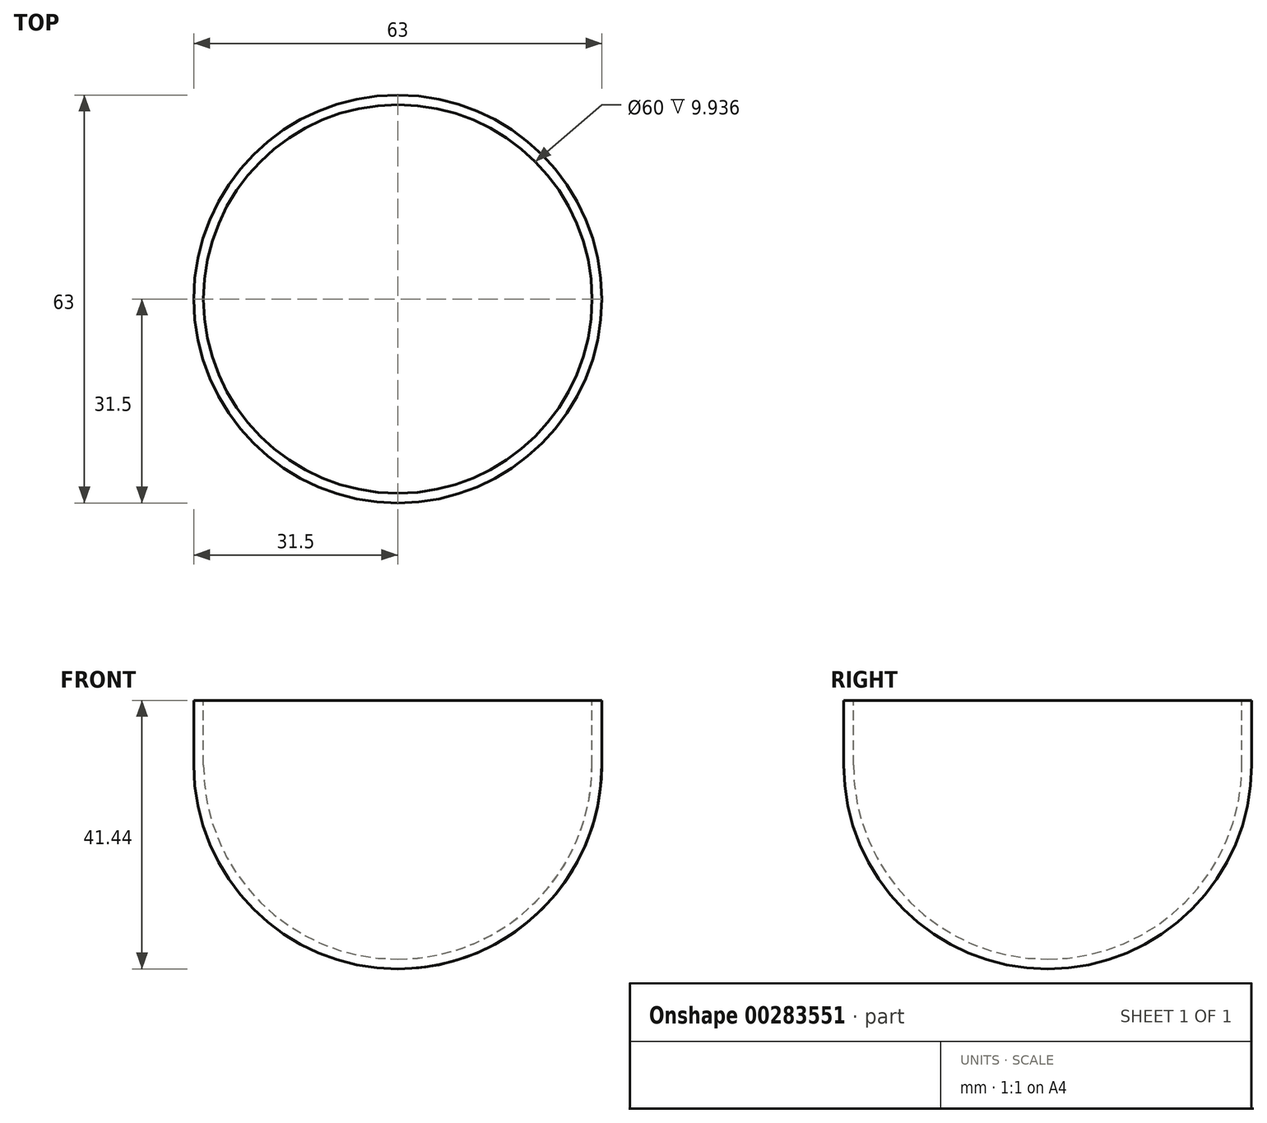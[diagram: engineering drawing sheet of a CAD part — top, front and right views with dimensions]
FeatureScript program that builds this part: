
annotation { "Feature Type Name" : "Feature", "Feature Type Description" : "" }
export const myFeature = defineFeature(function(context is Context, id is Id, definition is map)
    precondition{}
    {
        {
            var Q0;
            Q0=qCreatedBy(makeId("Front.planeOp"),FACE);
            var sketch = newSketch(context, id + "F0", { "sketchPlane" : qUnion([Q0])});
            skLineSegment(sketch, "E0", {"start": v(33, 33) * mm, "end": v(33, 50) * mm});
            skLineSegment(sketch, "E1", {"start": v(33, 33) * mm, "end": v(33, 0) * mm, "construction": true});
            skLineSegment(sketch, "E2", {"start": v(0, 75) * mm, "end": v(0, 33) * mm, "construction": true});
            skLineSegment(sketch, "E3", {"start": v(0, 0) * mm, "end": v(0, 6.53) * mm});
            skArc(sketch, "E4", {"start": v(0, 0) * mm, "mid": v(23.33, 9.67) * mm, "end": v(33, 33) * mm});
            skArc(sketch, "E5.0", {"start": v(0, 3) * mm, "mid": v(21.21, 11.79) * mm, "end": v(30, 33) * mm});
            skLineSegment(sketch, "E6", {"start": v(30, 33) * mm, "end": v(30, 50) * mm});
            skLineSegment(sketch, "E7", {"start": v(30, 50) * mm, "end": v(30, 50) * mm});
            skPoint(sketch, "E8.orphan", {"position": v(33, 50) * mm});
            skLineSegment(sketch, "E9", {"start": v(21.21, 11.79) * mm, "end": v(22.27, 10.73) * mm, "construction": true});
            skLineSegment(sketch, "E10", {"start": v(31.5, 33) * mm, "end": v(30, 33) * mm});
            skLineSegment(sketch, "E11", {"start": v(30, 50) * mm, "end": v(31.5, 50) * mm});
            skLineSegment(sketch, "E12", {"start": v(31.7, 50) * mm, "end": v(31.7, 55) * mm, "construction": true});
            skLineSegment(sketch, "E13", {"start": v(31.7, 55) * mm, "end": v(31.7, 72) * mm});
            skLineSegment(sketch, "E14", {"start": v(31.7, 72) * mm, "end": v(30.7, 72) * mm});
            skLineSegment(sketch, "E15", {"start": v(30.7, 72) * mm, "end": v(30.7, 55) * mm});
            skLineSegment(sketch, "E16", {"start": v(30.7, 55) * mm, "end": v(31.7, 55) * mm});
            skLineSegment(sketch, "E17", {"start": v(31.7, 63.5) * mm, "end": v(22.7, 63.5) * mm, "construction": true});
            skPoint(sketch, "E17.endSnap0", {"position": v(31.7, 63.5) * mm});
            skLineSegment(sketch, "E18", {"start": v(22.7, 63.5) * mm, "end": v(22.7, 72) * mm});
            skLineSegment(sketch, "E19", {"start": v(22.7, 63.5) * mm, "end": v(22.7, 55) * mm});
            skLineSegment(sketch, "E20", {"start": v(22.7, 55) * mm, "end": v(23.7, 55) * mm});
            skLineSegment(sketch, "E21", {"start": v(23.7, 55) * mm, "end": v(23.7, 63.5) * mm});
            skLineSegment(sketch, "E22", {"start": v(22.7, 55) * mm, "end": v(22.2, 55) * mm});
            skLineSegment(sketch, "E23", {"start": v(22.2, 55) * mm, "end": v(22.2, 72) * mm});
            skLineSegment(sketch, "E24", {"start": v(22.2, 72) * mm, "end": v(22.7, 72) * mm});
            skArc(sketch, "E25", {"start": v(0, 31.3) * mm, "mid": v(16.76, 38.24) * mm, "end": v(23.7, 55) * mm});
            skArc(sketch, "E26.0", {"start": v(0, 32.8) * mm, "mid": v(15.7, 39.3) * mm, "end": v(22.2, 55) * mm});
            skLineSegment(sketch, "E27", {"start": v(0, 32.8) * mm, "end": v(0, 31.3) * mm});
            skLineSegment(sketch, "E28", {"start": v(31.5, 33) * mm, "end": v(31.7, 33) * mm});
            skLineSegment(sketch, "E29", {"start": v(31.7, 33) * mm, "end": v(31.7, 50) * mm});
            skLineSegment(sketch, "E30.trimOffspring", {"start": v(0, 32.8) * mm, "end": v(0, 0) * mm, "construction": true});
            skLineSegment(sketch, "E31", {"start": v(23.7, 63.5) * mm, "end": v(23.7, 55) * mm});
            skLineSegment(sketch, "E32", {"start": v(23.7, 59.25) * mm, "end": v(28.8, 59.23) * mm, "construction": true});
            skLineSegment(sketch, "E33", {"start": v(23.7, 59.25) * mm, "end": v(25.4, 59.25) * mm, "construction": true});
            skLineSegment(sketch, "E34", {"start": v(23.64, 59.25) * mm, "end": v(25.34, 59.24) * mm, "construction": true});
            skLineSegment(sketch, "E35", {"start": v(25.4, 59.25) * mm, "end": v(25.4, 61.45) * mm, "construction": true});
            skLineSegment(sketch, "E36", {"start": v(23.64, 59.25) * mm, "end": v(23.64, 57.05) * mm, "construction": true});
            skFitSpline(sketch, "E37", {"points": [v(23.7, 59.25) * mm, v(24.3, 60.78) * mm, v(25.4, 61.45) * mm], "startDerivative": vector(0, 1.77) * mm, "endDerivative": vector(2.28, 0.15) * mm});
            skLineSegment(sketch, "E38", {"start": v(23.7, 59.25) * mm, "end": v(24.2, 59.25) * mm});
            skLineSegment(sketch, "E39", {"start": v(25.4, 61.45) * mm, "end": v(25.4, 60.95) * mm});
            skFitSpline(sketch, "E40", {"points": [v(24.2, 59.25) * mm, v(24.56, 60.34) * mm, v(25.4, 60.95) * mm], "startDerivative": vector(0.07, 1.51) * mm, "endDerivative": vector(2.13, 0.19) * mm});
            skFitSpline(sketch, "E41", {"points": [v(25.4, 60.95) * mm, v(26.43, 60.35) * mm, v(26.85, 59.25) * mm], "startDerivative": vector(2.26, -0.06) * mm, "endDerivative": vector(0.1, -2.09) * mm});
            skFitSpline(sketch, "E42", {"points": [v(25.4, 61.45) * mm, v(26.6, 60.89) * mm, v(27.35, 59.25) * mm], "startDerivative": vector(2.58, -0.22) * mm, "endDerivative": vector(-0.05, -2.13) * mm});
            skFitSpline(sketch, "E43.MirrorCS", {"points": [v(28.8, 57.55) * mm, v(27.77, 58.15) * mm, v(27.35, 59.25) * mm], "startDerivative": vector(-2.26, 0.06) * mm, "endDerivative": vector(-0.1, 2.09) * mm});
            skFitSpline(sketch, "E44.MirrorCS", {"points": [v(28.8, 57.05) * mm, v(27.6, 57.61) * mm, v(26.85, 59.25) * mm], "startDerivative": vector(-2.58, 0.22) * mm, "endDerivative": vector(0.05, 2.13) * mm});
            skFitSpline(sketch, "E45.MirrorCS", {"points": [v(30.29, 59.23) * mm, v(29.97, 58.34) * mm, v(28.8, 57.55) * mm], "startDerivative": vector(-0.07, -1.51) * mm, "endDerivative": vector(-2.13, -0.19) * mm});
            skFitSpline(sketch, "E46.MirrorCS", {"points": [v(30.7, 59.26) * mm, v(30.25, 58) * mm, v(28.8, 57.05) * mm], "startDerivative": vector(0, -1.77) * mm, "endDerivative": vector(-2.28, -0.15) * mm});
            skLineSegment(sketch, "E47", {"start": v(24.07, 58.94) * mm, "end": v(23.96, 58.52) * mm});
            skLineSegment(sketch, "E48", {"start": v(23.96, 58.52) * mm, "end": v(23.84, 58.07) * mm});
            skLineSegment(sketch, "E49", {"start": v(23.84, 58.07) * mm, "end": v(23.78, 57.67) * mm});
            skLineSegment(sketch, "E50", {"start": v(23.78, 57.67) * mm, "end": v(23.7, 57.12) * mm});
            skLineSegment(sketch, "E51", {"start": v(24.07, 58.94) * mm, "end": v(24.31, 59.78) * mm});
            skLineSegment(sketch, "E52", {"start": v(27.1, 59.25) * mm, "end": v(27.1, 57.68) * mm});
            skLineSegment(sketch, "E53", {"start": v(30.5, 59.71) * mm, "end": v(30.63, 60.43) * mm});
            skLineSegment(sketch, "E54", {"start": v(30.63, 60.43) * mm, "end": v(30.7, 61.23) * mm});
            skLineSegment(sketch, "E55", {"start": v(30.5, 59.71) * mm, "end": v(30.36, 59.23) * mm});
            skLineSegment(sketch, "E56", {"start": v(30.36, 59.23) * mm, "end": v(30.18, 58.73) * mm});
            skLineSegment(sketch, "E57", {"start": v(23.7, 63.5) * mm, "end": v(22.7, 63.5) * mm});
            skLineSegment(sketch, "E58", {"start": v(22.2, 72) * mm, "end": v(0, 72) * mm, "construction": true});
            skLineSegment(sketch, "E59", {"start": v(31.7, 33) * mm, "end": v(32, 33) * mm});
            skLineSegment(sketch, "E60", {"start": v(32, 33) * mm, "end": v(32, 50) * mm});
            skLineSegment(sketch, "E61", {"start": v(32, 50) * mm, "end": v(33, 50) * mm});
            skLineSegment(sketch, "E62", {"start": v(32, 33) * mm, "end": v(33, 33) * mm});
            skLineSegment(sketch, "E63", {"start": v(33, 38.12) * mm, "end": v(32, 38.12) * mm});
            skArc(sketch, "E64", {"start": v(0, 1.5) * mm, "mid": v(22.27, 10.73) * mm, "end": v(31.5, 33) * mm});
            skArc(sketch, "E65.trimOffspring", {"start": v(23.67, 53.79) * mm, "mid": v(22.95, 54.58) * mm, "end": v(22.2, 55.35) * mm});
            skLineSegment(sketch, "E66", {"start": v(31.5, 33) * mm, "end": v(31.5, 42.94) * mm});
            skLineSegment(sketch, "E67", {"start": v(31.5, 42.94) * mm, "end": v(30, 42.94) * mm});
            skSolve(sketch);
        }
        {
            var Q0;
            {var subQ0=sQuery(id+"F0.wireOp",EDGE,"E5.0");Q0=makeQuery(id+"F0.imprint","IMPRINT",FACE,{"disambiguationData":[TD([[makeQuery(id+"F0.imprint","IMPRINT",EDGE,{"derivedFrom":subQ0}),-1.0]])]});}
            var Q1;
            {var subQ0=sQuery(id+"F0.wireOp",EDGE,"E10");Q1=makeQuery(id+"F0.imprint","IMPRINT",FACE,{"disambiguationData":[TD([[makeQuery(id+"F0.imprint","IMPRINT",EDGE,{"derivedFrom":subQ0}),-1.0]])]});}
            var Q2;
            Q2=sQuery(id+"F0.wireOp",EDGE,"E2");
            revolve(context, id + "F1", {"entities" : qUnion([Q0, Q1]), "axis" : qUnion([Q2]), "revolveType" : RevolveType.FULL});
        }
    });
